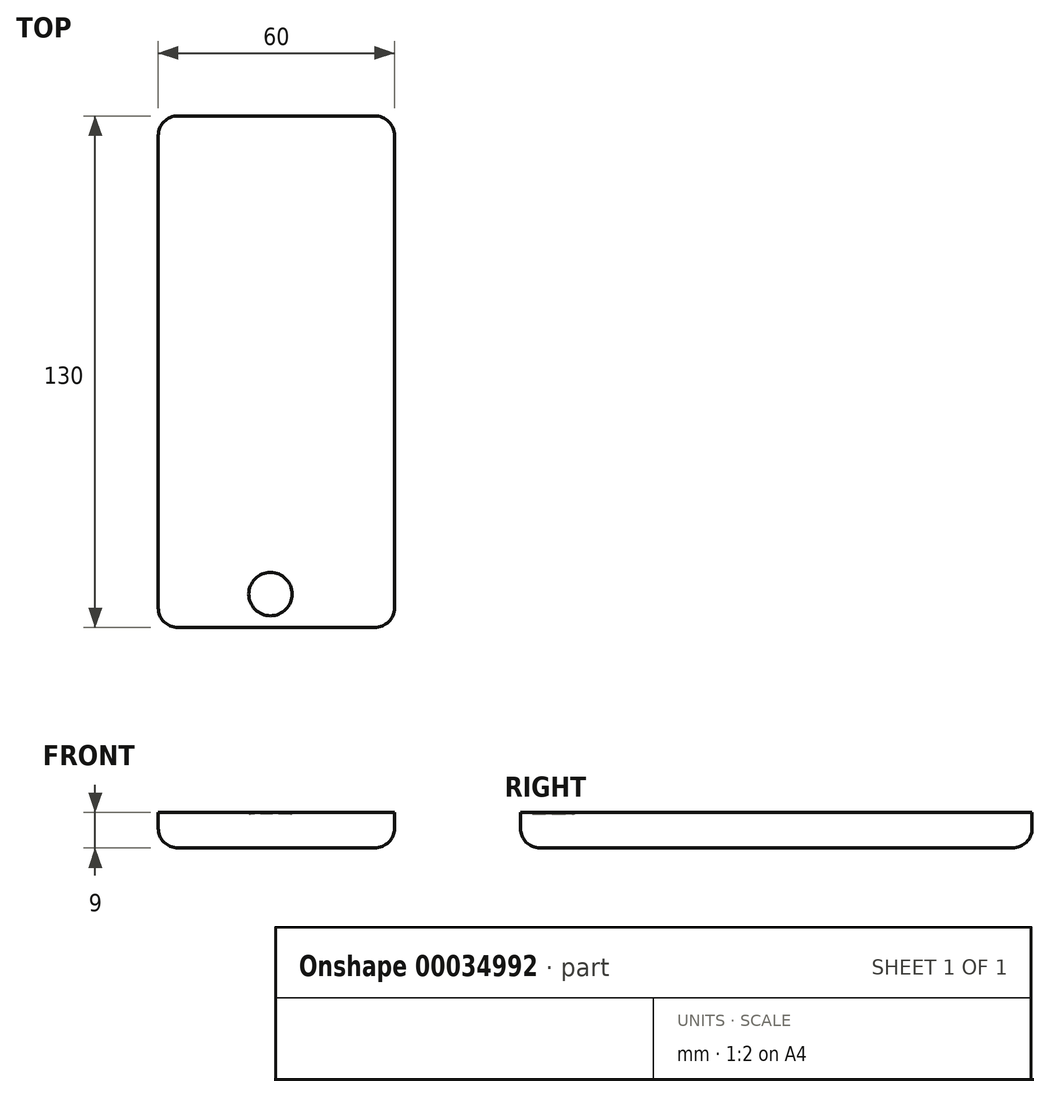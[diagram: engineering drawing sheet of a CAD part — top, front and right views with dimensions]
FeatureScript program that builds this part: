
annotation { "Feature Type Name" : "Feature", "Feature Type Description" : "" }
export const myFeature = defineFeature(function(context is Context, id is Id, definition is map)
    precondition{}
    {
        {
            var Q0;
            Q0=qCreatedBy(makeId("Top.planeOp"),FACE);
            var sketch = newSketch(context, id + "F0", { "sketchPlane" : qUnion([Q0])});
            skLineSegment(sketch, "E0.bottom", {"start": v(-43.62, 63.93) * mm, "end": v(16.38, 63.93) * mm});
            skLineSegment(sketch, "E0.top", {"start": v(-43.62, -66.07) * mm, "end": v(16.38, -66.07) * mm});
            skLineSegment(sketch, "E0.left", {"start": v(-43.62, 63.93) * mm, "end": v(-43.62, -66.07) * mm});
            skLineSegment(sketch, "E0.right", {"start": v(16.38, 63.93) * mm, "end": v(16.38, -66.07) * mm});
            skSolve(sketch);
        }
        {
            var Q0;
            Q0=makeQuery(id+"F0.imprint","IMPRINT",FACE,{"disambiguationData":[TD([[makeQuery(id+"F0.imprint","IMPRINT",EDGE,{"derivedFrom":sQuery(id+"F0.wireOp",EDGE,"E0.bottom")}),-1.0]])]});
            extrude(context, id + "F1", {"entities" : qUnion([Q0]), "depth" : 9 * mm});
        }
        {
            var Q0;
            Q0=makeQuery(id+"F1.opExtrude","CAP_EDGE",EDGE,{"disambiguationData":[OSD([sQuery(id+"F0.wireOp",EDGE,"E0.right")])],"isStart":true});
            fillet(context, id + "F2", {"entities" : qUnion([Q0]), "radius" : 5 * mm, "tangentPropagation" : true, "allowEdgeOverflow" : false});
        }
        {
            var Q0;
            Q0=makeQuery(id+"F1.opExtrude","CAP_EDGE",EDGE,{"disambiguationData":[OSD([sQuery(id+"F0.wireOp",EDGE,"E0.left")])],"isStart":true});
            fillet(context, id + "F3", {"entities" : qUnion([Q0]), "radius" : 5 * mm, "tangentPropagation" : true, "allowEdgeOverflow" : false});
        }
        {
            var Q0;
            Q0=makeQuery(id+"F1.opExtrude","CAP_EDGE",EDGE,{"disambiguationData":[OSD([sQuery(id+"F0.wireOp",EDGE,"E0.bottom")])],"isStart":true});
            fillet(context, id + "F4", {"entities" : qUnion([Q0]), "radius" : 5 * mm, "tangentPropagation" : true, "allowEdgeOverflow" : false});
        }
        {
            var Q0;
            Q0=makeQuery(id+"F1.opExtrude","CAP_EDGE",EDGE,{"disambiguationData":[OSD([sQuery(id+"F0.wireOp",EDGE,"E0.top")])],"isStart":true});
            fillet(context, id + "F5", {"entities" : qUnion([Q0]), "radius" : 5 * mm, "tangentPropagation" : true, "allowEdgeOverflow" : false});
        }
        {
            var Q0;
            Q0=makeQuery(id+"F1.opExtrude","CAP_FACE",FACE,{"disambiguationData":[OSD([sQuery(id+"F0.wireOp",EDGE,"E0.bottom"),sQuery(id+"F0.wireOp",EDGE,"E0.top"),sQuery(id+"F0.wireOp",EDGE,"E0.left"),sQuery(id+"F0.wireOp",EDGE,"E0.right")])],"isStart":false});
            var sketch = newSketch(context, id + "F6", { "sketchPlane" : qUnion([Q0])});
            skCircle(sketch, "E1", {"center": v(-15.12, -57.57) * mm, "radius": 5.5 * mm});
            skSolve(sketch);
        }
        {
            var Q0;
            Q0=makeQuery(id+"F6.imprint","IMPRINT",FACE,{"disambiguationData":[TD([[makeQuery(id+"F6.imprint","IMPRINT",EDGE,{"derivedFrom":sQuery(id+"F6.wireOp",EDGE,"E1")}),1.0]])]});
            extrude(context, id + "F7", {"entities" : qUnion([Q0]), "operationType" : NewBodyOperationType.REMOVE, "oppositeDirection" : true, "depth" : 0.4 * mm});
        }
        {
            var Q0;
            Q0=makeQuery(id+"F7.boolean.opBoolean","COPY",EDGE,{"derivedFrom":makeQuery(id+"F7.opExtrude","CAP_EDGE",EDGE,{"disambiguationData":[OSD([sQuery(id+"F6.wireOp",EDGE,"E1")])],"isStart":false})});
            fillet(context, id + "F8", {"entities" : qUnion([Q0]), "radius" : 0.4 * mm, "tangentPropagation" : true, "allowEdgeOverflow" : false});
        }
    });
